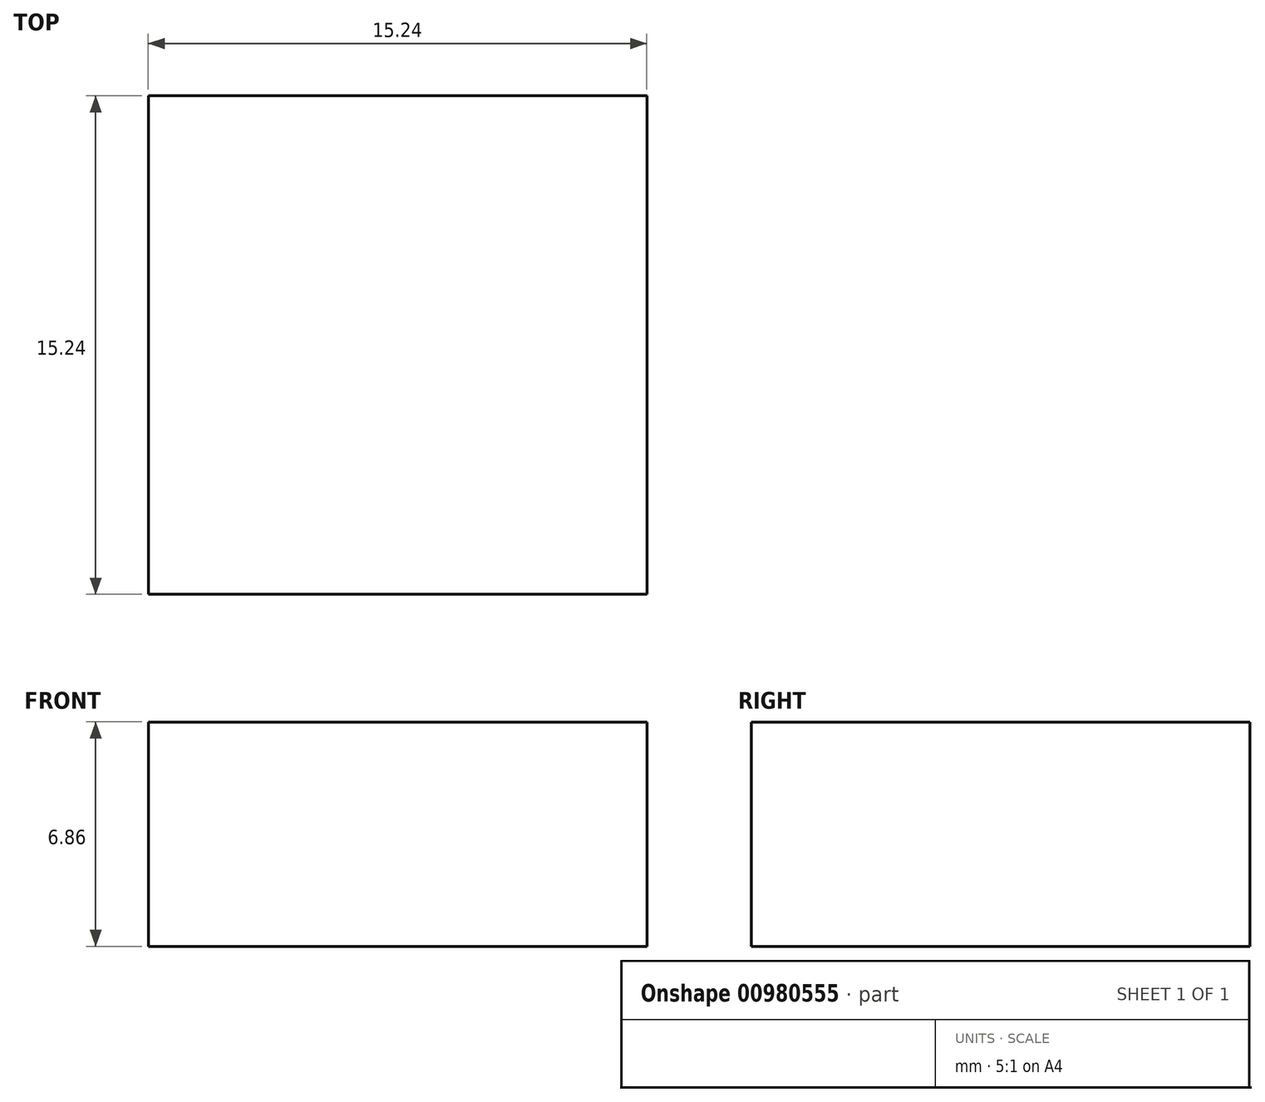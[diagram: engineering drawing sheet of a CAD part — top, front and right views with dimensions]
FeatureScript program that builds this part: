
annotation { "Feature Type Name" : "Feature", "Feature Type Description" : "" }
export const myFeature = defineFeature(function(context is Context, id is Id, definition is map)
    precondition{}
    {
        {
            var Q0;
            Q0=qCreatedBy(makeId("Top.planeOp"),FACE);
            var sketch = newSketch(context, id + "F0", { "sketchPlane" : qUnion([Q0])});
            skLineSegment(sketch, "E0.bottom", {"start": v(7.8, -7.62) * mm, "end": v(-7.45, -7.62) * mm});
            skLineSegment(sketch, "E0.top", {"start": v(7.8, 7.62) * mm, "end": v(-7.45, 7.62) * mm});
            skLineSegment(sketch, "E0.left", {"start": v(7.8, -7.62) * mm, "end": v(7.8, 7.62) * mm});
            skLineSegment(sketch, "E0.right", {"start": v(-7.45, -7.62) * mm, "end": v(-7.45, 7.62) * mm});
            skPoint(sketch, "E0.middle", {"position": v(0.17, 0) * mm});
            skSolve(sketch);
        }
        {
            var Q0;
            Q0=makeQuery(id+"F0.imprint","IMPRINT",FACE,{"disambiguationData":[TD([[makeQuery(id+"F0.imprint","IMPRINT",EDGE,{"derivedFrom":sQuery(id+"F0.wireOp",EDGE,"E0.bottom")}),-1.0]])]});
            extrude(context, id + "F1", {"entities" : qUnion([Q0]), "depth" : 6.86 * mm, "offsetDistance" : 25.4 * mm});
        }
    });
